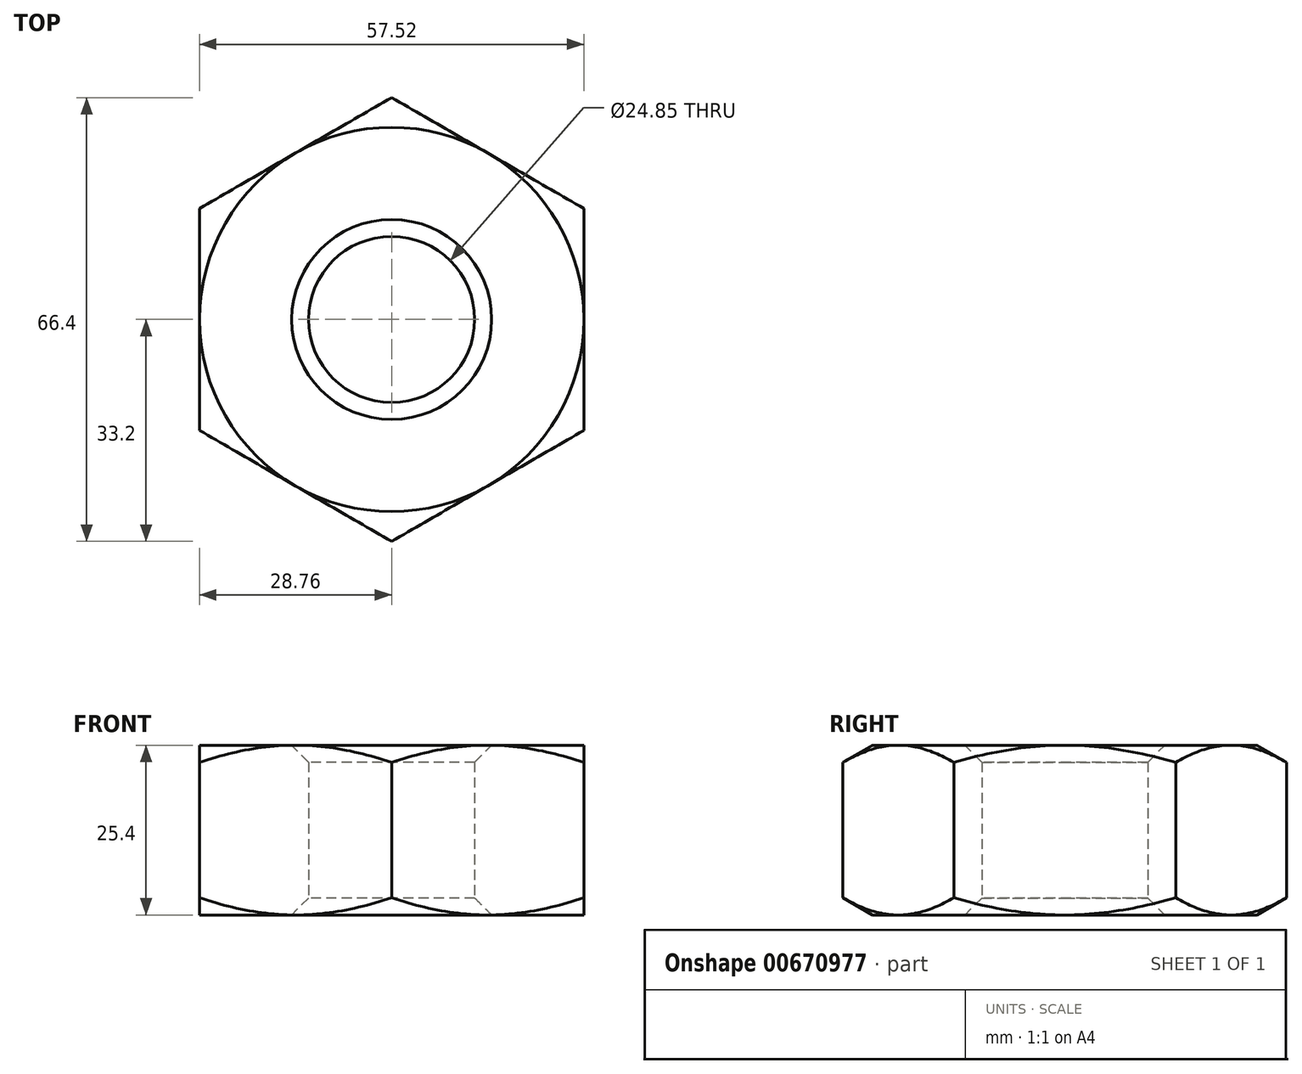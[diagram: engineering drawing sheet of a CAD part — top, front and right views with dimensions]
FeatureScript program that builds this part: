
annotation { "Feature Type Name" : "Feature", "Feature Type Description" : "" }
export const myFeature = defineFeature(function(context is Context, id is Id, definition is map)
    precondition{}
    {
        {
            var Q0;
            Q0=qCreatedBy(makeId("Top.planeOp"),FACE);
            var sketch = newSketch(context, id + "F0", { "sketchPlane" : qUnion([Q0])});
            skCircle(sketch, "E0.cCircle", {"center": v(0, 0) * mm, "radius": 28.76 * mm, "construction": true});
            skLineSegment(sketch, "E0.0", {"start": v(-28.76, -16.6) * mm, "end": v(-28.76, 16.6) * mm});
            skLineSegment(sketch, "E0.1", {"start": v(-28.76, 16.6) * mm, "end": v(0, 33.2) * mm});
            skLineSegment(sketch, "E0.2", {"start": v(0, 33.2) * mm, "end": v(28.76, 16.6) * mm});
            skLineSegment(sketch, "E0.3", {"start": v(28.76, 16.6) * mm, "end": v(28.76, -16.6) * mm});
            skLineSegment(sketch, "E0.4", {"start": v(28.76, -16.6) * mm, "end": v(0, -33.2) * mm});
            skLineSegment(sketch, "E0.5", {"start": v(0, -33.2) * mm, "end": v(-28.76, -16.6) * mm});
            skPoint(sketch, "E0.0.midPoint", {"position": v(-28.76, 0) * mm});
            skCircle(sketch, "E1", {"center": v(0, 0) * mm, "radius": 12.42 * mm});
            skSolve(sketch);
        }
        {
            var Q0;
            Q0 = qSketchRegion(id + "F0", true);
            extrude(context, id + "F1", {"entities" : qUnion([Q0]), "depth" : 25.4 * mm, "offsetDistance" : 25.4 * mm});
        }
        {
            var Q0;
            Q0=qCreatedBy(makeId("Front.planeOp"),FACE);
            var sketch = newSketch(context, id + "F2", { "sketchPlane" : qUnion([Q0])});
            skLineSegment(sketch, "E2", {"start": v(0, 0) * mm, "end": v(0, 25.4) * mm, "construction": true});
            skLineSegment(sketch, "E3", {"start": v(0, 12.7) * mm, "end": v(-28.82, 12.7) * mm, "construction": true});
            skLineSegment(sketch, "E4", {"start": v(-28.76, 25.4) * mm, "end": v(-47.01, 25.4) * mm});
            skLineSegment(sketch, "E5", {"start": v(-28.76, 25.4) * mm, "end": v(-47.01, 14.86) * mm});
            skLineSegment(sketch, "E6", {"start": v(-47.01, 14.86) * mm, "end": v(-47.01, 25.4) * mm});
            skLineSegment(sketch, "E7.MirrorCS", {"start": v(-28.76, 0) * mm, "end": v(-47.01, 0) * mm});
            skLineSegment(sketch, "E8.MirrorCS", {"start": v(-47.01, 10.54) * mm, "end": v(-47.01, 0) * mm});
            skLineSegment(sketch, "E9.MirrorCS", {"start": v(-28.76, 0) * mm, "end": v(-47.01, 10.54) * mm});
            skSolve(sketch);
        }
        {
            var Q0;
            Q0 = qSketchRegion(id + "F2", true);
            var Q1;
            Q1=sQuery(id+"F2.wireOp",EDGE,"E2");
            revolve(context, id + "F3", {"operationType" : NewBodyOperationType.REMOVE, "entities" : qUnion([Q0]), "axis" : qUnion([Q1]), "revolveType" : RevolveType.FULL, "oppositeDirection" : true});
        }
        {
            var Q0;
            Q0=makeQuery(id+"F1.opExtrude","CAP_EDGE",EDGE,{"disambiguationData":[OSD([sQuery(id+"F0.wireOp",EDGE,"E1")])],"isStart":false});
            chamfer(context, id + "F4", {"entities" : qUnion([Q0]), "width" : 2.54 * mm, "tangentPropagation" : true});
        }
        {
            var Q0;
            Q0=makeQuery(id+"F1.opExtrude","CAP_EDGE",EDGE,{"disambiguationData":[OSD([sQuery(id+"F0.wireOp",EDGE,"E1")])],"isStart":true});
            chamfer(context, id + "F5", {"entities" : qUnion([Q0]), "width" : 2.54 * mm, "tangentPropagation" : true});
        }
    });
